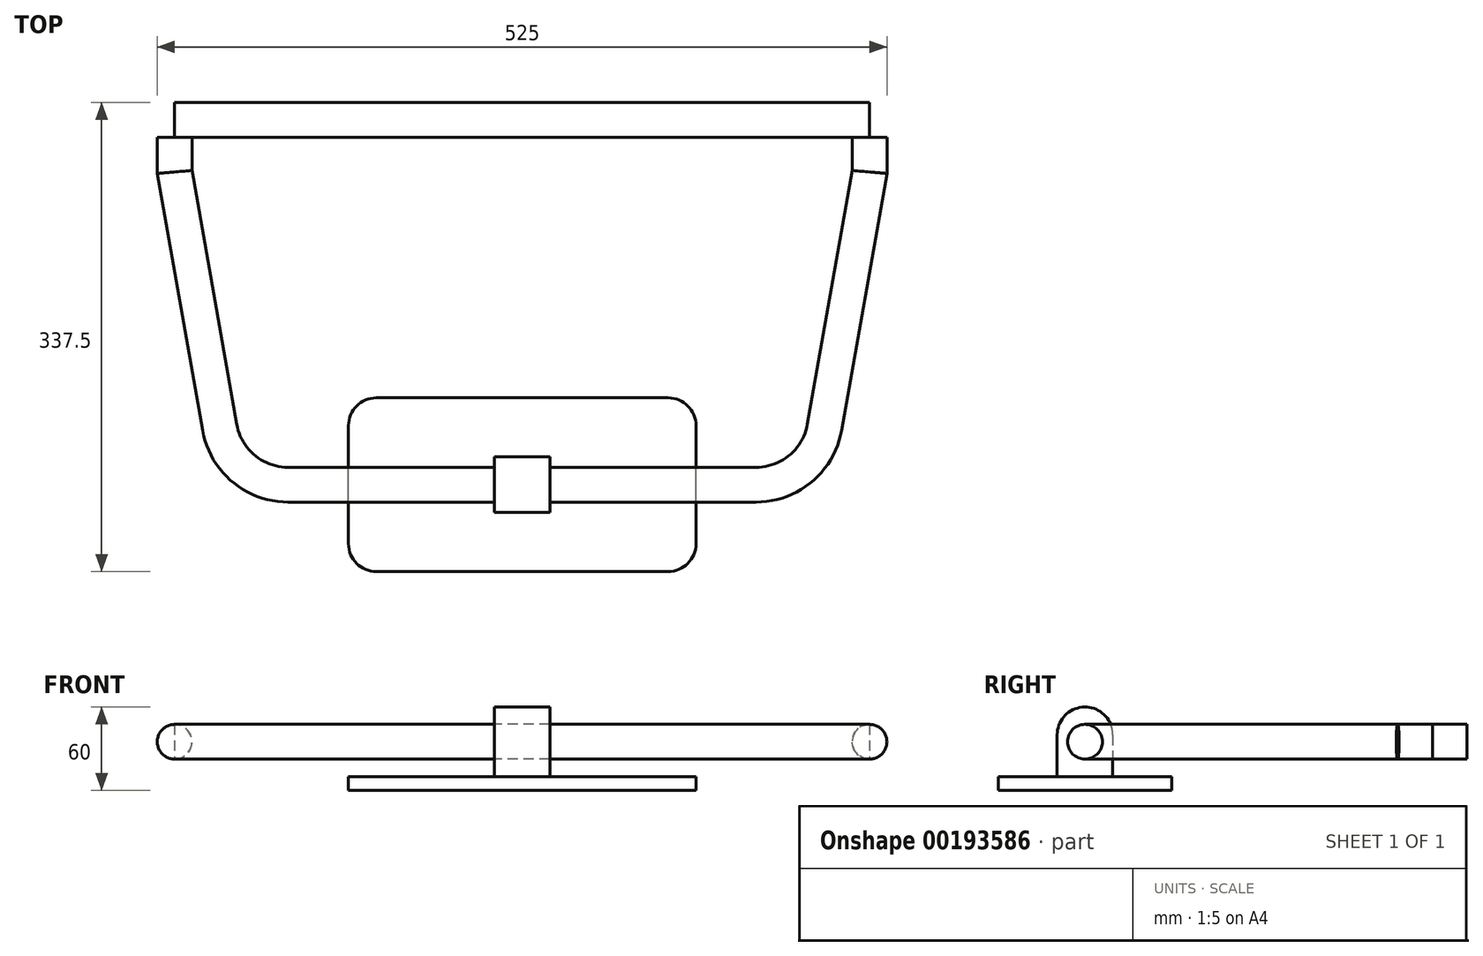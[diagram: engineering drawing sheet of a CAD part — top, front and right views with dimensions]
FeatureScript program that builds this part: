
annotation { "Feature Type Name" : "Feature", "Feature Type Description" : "" }
export const myFeature = defineFeature(function(context is Context, id is Id, definition is map)
    precondition{}
    {
        {
            var Q0;
            Q0=qCreatedBy(makeId("Front.planeOp"),FACE);
            var sketch = newSketch(context, id + "F0", { "sketchPlane" : qUnion([Q0])});
            skCircle(sketch, "E0", {"center": v(-465.65, 0) * mm, "radius": 12.5 * mm});
            skCircle(sketch, "E1", {"center": v(34.35, 0) * mm, "radius": 12.5 * mm});
            skSolve(sketch);
        }
        {
            var Q0;
            Q0=qCreatedBy(makeId("Top.planeOp"),FACE);
            var sketch = newSketch(context, id + "F1", { "sketchPlane" : qUnion([Q0])});
            skLineSegment(sketch, "E2", {"start": v(-465.65, 0) * mm, "end": v(-465.65, -25) * mm});
            skLineSegment(sketch, "E3", {"start": v(-465.65, -25) * mm, "end": v(-433.26, -208.68) * mm});
            skLineSegment(sketch, "E4", {"start": v(-384.02, -250) * mm, "end": v(-47.28, -250) * mm});
            skLineSegment(sketch, "E5", {"start": v(1.96, -208.68) * mm, "end": v(34.35, -25) * mm});
            skLineSegment(sketch, "E6", {"start": v(34.35, -25) * mm, "end": v(34.35, 0) * mm});
            skLineSegment(sketch, "E7", {"start": v(-465.65, 0) * mm, "end": v(34.35, 0) * mm, "construction": true});
            skPoint(sketch, "E8.visualSharp", {"position": v(-425.98, -250) * mm});
            skArc(sketch, "E8.filletArc", {"start": v(-433.26, -208.68) * mm, "mid": v(-416.16, -238.3) * mm, "end": v(-384.02, -250) * mm});
            skPoint(sketch, "E9.visualSharp", {"position": v(-5.33, -250) * mm});
            skArc(sketch, "E9.filletArc", {"start": v(-47.28, -250) * mm, "mid": v(-15.14, -238.3) * mm, "end": v(1.96, -208.68) * mm});
            skLineSegment(sketch, "E10", {"start": v(-433.26, -208.68) * mm, "end": v(1.96, -208.68) * mm, "construction": true});
            skSolve(sketch);
        }
        {
            var Q0;
            Q0=makeQuery(id+"F0.imprint","IMPRINT",FACE,{"disambiguationData":[TD([[makeQuery(id+"F0.imprint","IMPRINT",EDGE,{"derivedFrom":sQuery(id+"F0.wireOp",EDGE,"E0")}),1.0]])]});
            var Q1;
            Q1=sQuery(id+"F1.wireOp",EDGE,"E2");
            var Q2;
            Q2=sQuery(id+"F1.wireOp",EDGE,"E3");
            var Q3;
            Q3=sQuery(id+"F1.wireOp",EDGE,"E8.filletArc");
            var Q4;
            Q4=sQuery(id+"F1.wireOp",EDGE,"E4");
            var Q5;
            Q5=sQuery(id+"F1.wireOp",EDGE,"E9.filletArc");
            var Q6;
            Q6=sQuery(id+"F1.wireOp",EDGE,"E5");
            var Q7;
            Q7=sQuery(id+"F1.wireOp",EDGE,"E6");
            sweep(context, id + "F2", {"profiles" : qUnion([Q0]), "path" : qUnion([Q1, Q2, Q3, Q4, Q5, Q6, Q7])});
        }
        {
            var Q0;
            Q0=makeQuery(id+"F2.opSweep","CAP_FACE",FACE,{"disambiguationData":[OSD([sQuery(id+"F0.wireOp",EDGE,"E0"),sQuery(id+"F1.wireOp",VERTEX,"E2.start")])],"isStart":true});
            var sketch = newSketch(context, id + "F3", { "sketchPlane" : qUnion([Q0])});
            skLineSegment(sketch, "E11.bottom", {"start": v(-34.35, 12.5) * mm, "end": v(465.65, 12.5) * mm});
            skLineSegment(sketch, "E11.top", {"start": v(-34.35, -12.5) * mm, "end": v(465.65, -12.5) * mm});
            skLineSegment(sketch, "E11.left", {"start": v(-34.35, 12.5) * mm, "end": v(-34.35, -12.5) * mm});
            skLineSegment(sketch, "E11.right", {"start": v(465.65, 12.5) * mm, "end": v(465.65, -12.5) * mm});
            skLineSegment(sketch, "E12", {"start": v(-58.64, 0) * mm, "end": v(490.52, 0) * mm, "construction": true});
            skSolve(sketch);
        }
        {
            var Q0;
            {var subQ0=sQuery(id+"F3.wireOp",EDGE,"E11.bottom");Q0=makeQuery(id+"F3.imprint","IMPRINT",FACE,{"disambiguationData":[TD([[makeQuery(id+"F3.imprint","IMPRINT",EDGE,{"derivedFrom":subQ0}),-1.0]])]});}
            var Q1;
            {var subQ0=sQuery(id+"F3.wireOp",EDGE,"E11.right");Q1=makeQuery(id+"F3.imprint","IMPRINT",FACE,{"disambiguationData":[TD([[makeQuery(id+"F3.imprint","IMPRINT",EDGE,{"derivedFrom":subQ0}),-1.0]])]});}
            extrude(context, id + "F4", {"entities" : qUnion([Q0, Q1]), "operationType" : NewBodyOperationType.ADD, "depth" : 25 * mm});
        }
        {
            var Q0;
            Q0=qCreatedBy(makeId("Top.planeOp"),FACE);
            var sketch = newSketch(context, id + "F5", { "sketchPlane" : qUnion([Q0])});
            skLineSegment(sketch, "E13.bottom", {"start": v(-235.52, -230) * mm, "end": v(-195.52, -230) * mm});
            skLineSegment(sketch, "E13.top", {"start": v(-235.52, -270) * mm, "end": v(-195.52, -270) * mm});
            skLineSegment(sketch, "E13.left", {"start": v(-235.52, -230) * mm, "end": v(-235.52, -270) * mm});
            skLineSegment(sketch, "E13.right", {"start": v(-195.52, -230) * mm, "end": v(-195.52, -270) * mm});
            skLineSegment(sketch, "E14", {"start": v(-484.27, -250) * mm, "end": v(59.34, -250) * mm, "construction": true});
            skLineSegment(sketch, "E15", {"start": v(-215.52, -295.86) * mm, "end": v(-215.52, -124.77) * mm, "construction": true});
            skSolve(sketch);
        }
        {
            var Q0;
            Q0=makeQuery(id+"F5.imprint","IMPRINT",FACE,{"disambiguationData":[TD([[makeQuery(id+"F5.imprint","IMPRINT",EDGE,{"derivedFrom":sQuery(id+"F5.wireOp",EDGE,"E13.bottom")}),-1.0]])]});
            extrude(context, id + "F6", {"entities" : qUnion([Q0]), "operationType" : NewBodyOperationType.ADD, "depth" : 25 * mm, "hasSecondDirection" : true, "secondDirectionOppositeDirection" : true, "secondDirectionDepth" : 25 * mm});
        }
        {
            var Q0;
            Q0=makeQuery(id+"F6.opExtrude","CAP_EDGE",EDGE,{"disambiguationData":[OSD([sQuery(id+"F5.wireOp",EDGE,"E13.bottom")])],"isStart":false});
            var Q1;
            Q1=makeQuery(id+"F6.opExtrude","CAP_EDGE",EDGE,{"disambiguationData":[OSD([sQuery(id+"F5.wireOp",EDGE,"E13.top")])],"isStart":false});
            fillet(context, id + "F7", {"entities" : qUnion([Q0, Q1]), "radius" : 20 * mm, "tangentPropagation" : true, "allowEdgeOverflow" : false});
        }
        {
            var Q0;
            Q0=makeQuery(id+"F6.opExtrude","CAP_FACE",FACE,{"disambiguationData":[OSD([sQuery(id+"F5.wireOp",EDGE,"E13.bottom"),sQuery(id+"F5.wireOp",EDGE,"E13.top"),sQuery(id+"F5.wireOp",EDGE,"E13.left"),sQuery(id+"F5.wireOp",EDGE,"E13.right")])],"isStart":true});
            var sketch = newSketch(context, id + "F8", { "sketchPlane" : qUnion([Q0])});
            skLineSegment(sketch, "E16", {"start": v(-215.52, 169.77) * mm, "end": v(-215.52, 333.01) * mm, "construction": true});
            skLineSegment(sketch, "E17", {"start": v(108.97, 250) * mm, "end": v(-479.15, 250) * mm, "construction": true});
            skLineSegment(sketch, "E18.bottom", {"start": v(-320.52, 312.5) * mm, "end": v(-110.52, 312.5) * mm});
            skLineSegment(sketch, "E18.top", {"start": v(-320.52, 187.5) * mm, "end": v(-110.52, 187.5) * mm});
            skLineSegment(sketch, "E18.left", {"start": v(-340.52, 292.5) * mm, "end": v(-340.52, 207.5) * mm});
            skLineSegment(sketch, "E18.right", {"start": v(-90.52, 292.5) * mm, "end": v(-90.52, 207.5) * mm});
            skPoint(sketch, "E19.visualSharp", {"position": v(-90.52, 187.5) * mm});
            skArc(sketch, "E19.filletArc", {"start": v(-110.52, 187.5) * mm, "mid": v(-96.38, 193.36) * mm, "end": v(-90.52, 207.5) * mm});
            skPoint(sketch, "E20.visualSharp", {"position": v(-90.52, 312.5) * mm});
            skArc(sketch, "E20.filletArc", {"start": v(-90.52, 292.5) * mm, "mid": v(-96.38, 306.64) * mm, "end": v(-110.52, 312.5) * mm});
            skPoint(sketch, "E21.visualSharp", {"position": v(-340.52, 312.5) * mm});
            skArc(sketch, "E21.filletArc", {"start": v(-320.52, 312.5) * mm, "mid": v(-334.67, 306.64) * mm, "end": v(-340.52, 292.5) * mm});
            skPoint(sketch, "E22.visualSharp", {"position": v(-340.52, 187.5) * mm});
            skArc(sketch, "E22.filletArc", {"start": v(-340.52, 207.5) * mm, "mid": v(-334.67, 193.36) * mm, "end": v(-320.52, 187.5) * mm});
            skSolve(sketch);
        }
        {
            var Q0;
            Q0 = qSketchRegion(id + "F8", true);
            extrude(context, id + "F9", {"entities" : qUnion([Q0]), "operationType" : NewBodyOperationType.ADD, "depth" : 10 * mm});
        }
    });
